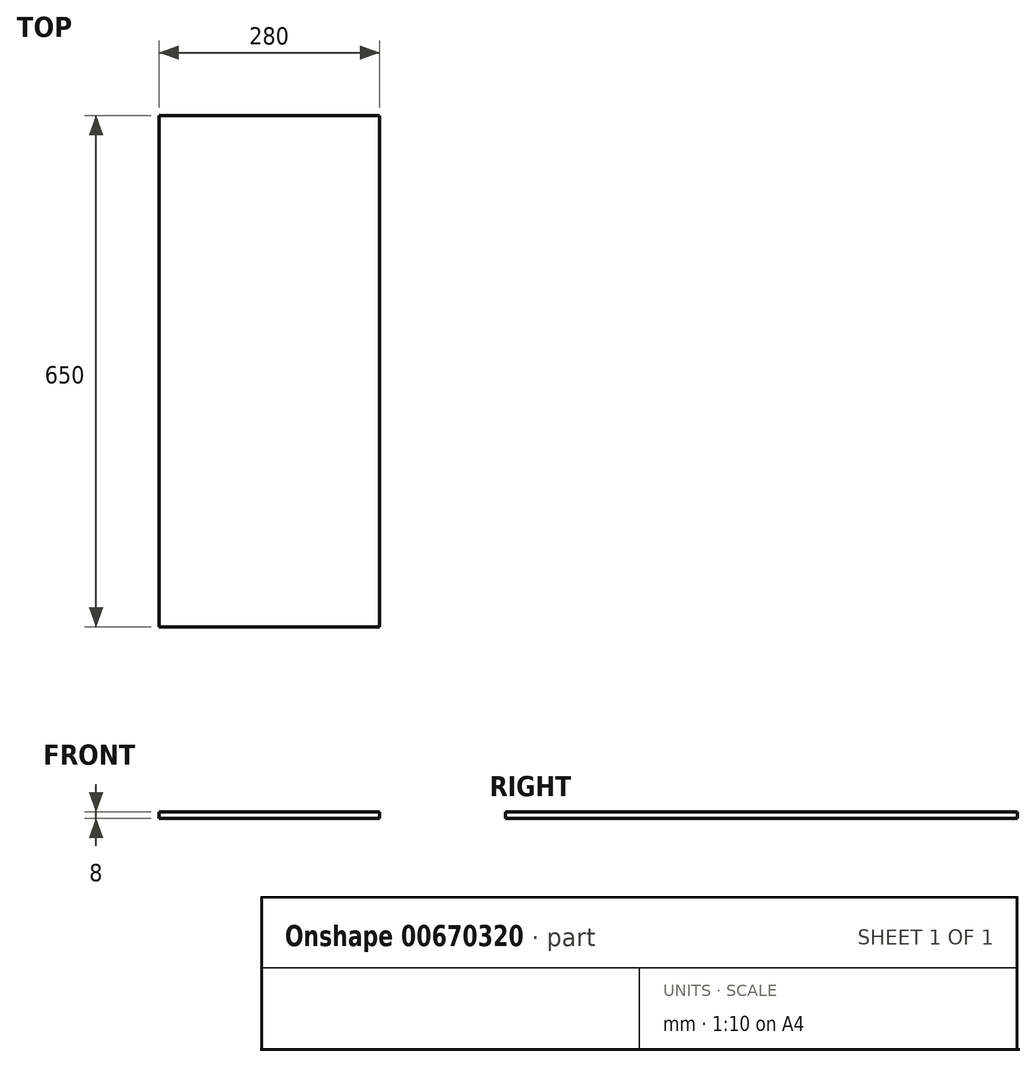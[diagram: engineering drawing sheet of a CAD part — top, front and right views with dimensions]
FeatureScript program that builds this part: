
annotation { "Feature Type Name" : "Feature", "Feature Type Description" : "" }
export const myFeature = defineFeature(function(context is Context, id is Id, definition is map)
    precondition{}
    {
        {
            var Q0;
            Q0=qCreatedBy(makeId("Top.planeOp"),FACE);
            var sketch = newSketch(context, id + "F0", { "sketchPlane" : qUnion([Q0])});
            skLineSegment(sketch, "E0", {"start": v(0, 0) * mm, "end": v(0, 650) * mm});
            skLineSegment(sketch, "E1", {"start": v(0, 650) * mm, "end": v(-280, 650) * mm});
            skLineSegment(sketch, "E2", {"start": v(-280, 650) * mm, "end": v(-280, 0) * mm});
            skLineSegment(sketch, "E3", {"start": v(-280, 0) * mm, "end": v(0, 0) * mm});
            skSolve(sketch);
        }
        {
            var Q0;
            Q0=makeQuery(id+"F0.imprint","IMPRINT",FACE,{"disambiguationData":[TD([[makeQuery(id+"F0.imprint","IMPRINT",EDGE,{"derivedFrom":sQuery(id+"F0.wireOp",EDGE,"E0")}),1.0]])]});
            extrude(context, id + "F1", {"entities" : qUnion([Q0]), "depth" : 8 * mm, "offsetDistance" : 25 * mm});
        }
    });
